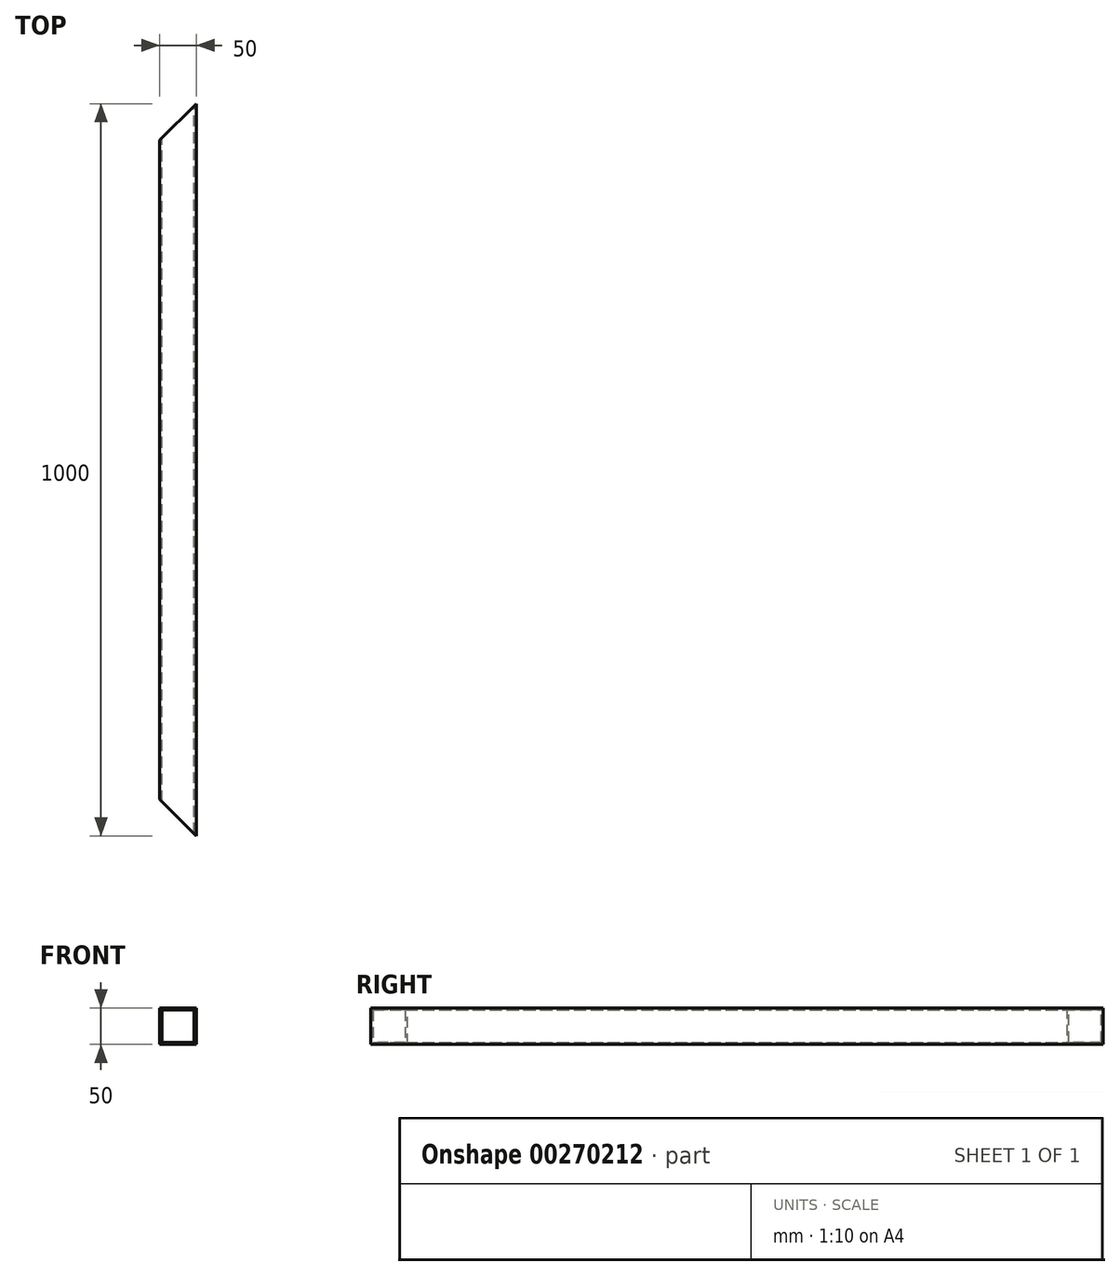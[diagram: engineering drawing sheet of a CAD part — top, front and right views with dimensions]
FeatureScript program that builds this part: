
annotation { "Feature Type Name" : "Feature", "Feature Type Description" : "" }
export const myFeature = defineFeature(function(context is Context, id is Id, definition is map)
    precondition{}
    {
        {
            var Q0;
            Q0=qCreatedBy(makeId("Front.planeOp"),FACE);
            var sketch = newSketch(context, id + "F0", { "sketchPlane" : qUnion([Q0])});
            skLineSegment(sketch, "E0.bottom", {"start": v(25, -25) * mm, "end": v(-25, -25) * mm});
            skLineSegment(sketch, "E0.top", {"start": v(25, 25) * mm, "end": v(-25, 25) * mm});
            skLineSegment(sketch, "E0.left", {"start": v(25, -25) * mm, "end": v(25, 25) * mm});
            skLineSegment(sketch, "E0.right", {"start": v(-25, -25) * mm, "end": v(-25, 25) * mm});
            skPoint(sketch, "E0.middle", {"position": v(0, 0) * mm});
            skLineSegment(sketch, "E1.bottom", {"start": v(22, -22) * mm, "end": v(-22, -22) * mm});
            skLineSegment(sketch, "E1.top", {"start": v(22, 22) * mm, "end": v(-22, 22) * mm});
            skLineSegment(sketch, "E1.left", {"start": v(22, -22) * mm, "end": v(22, 22) * mm});
            skLineSegment(sketch, "E1.right", {"start": v(-22, -22) * mm, "end": v(-22, 22) * mm});
            skSolve(sketch);
        }
        {
            var Q0;
            Q0=makeQuery(id+"F0.imprint","IMPRINT",FACE,{"disambiguationData":[TD([[makeQuery(id+"F0.imprint","IMPRINT",EDGE,{"derivedFrom":sQuery(id+"F0.wireOp",EDGE,"E0.bottom")}),-1.0]])]});
            extrude(context, id + "F1", {"entities" : qUnion([Q0]), "depth" : 1000 * mm});
        }
        {
            var Q0;
            Q0=makeQuery(id+"F1.opExtrude","CAP_EDGE",EDGE,{"disambiguationData":[OSD([sQuery(id+"F0.wireOp",EDGE,"E0.right")])],"isStart":false});
            var Q1;
            Q1=makeQuery(id+"F1.opExtrude","CAP_EDGE",EDGE,{"disambiguationData":[OSD([sQuery(id+"F0.wireOp",EDGE,"E0.right")])],"isStart":true});
            chamfer(context, id + "F2", {"entities" : qUnion([Q0, Q1]), "width" : 50 * mm, "tangentPropagation" : true});
        }
    });
